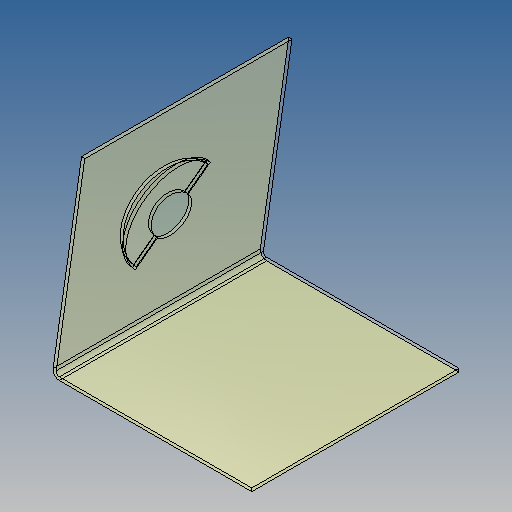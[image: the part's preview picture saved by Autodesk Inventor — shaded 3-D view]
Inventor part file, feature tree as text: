
AUTODESK INVENTOR PART (.ipt)
format: ipt  version: 2017 (Build 210142000, 142)  size: 194,560 bytes
history: native  units: mm
features: other x4, sketch x3, extrude x3, thicken_offset x1, sheet_metal_op x1, reference x1
ambient origin geometry x8: Origin, YZ Plane, XZ Plane, XY Plane, X Axis, Y Axis, Z Axis, Center Point
bodies: Solid1 (feature_tree)
feature tree (13):
  thicken_offset  "Thicken1"
  sketch  "Sketch2"  dims[d2=48.0mm d3=45.0mm]
  extrude  "Extrusion1"  Depth=49.0mm
  sheet_metal_op  "Fold1"
  extrude  "Extrusion2"  Depth=45.0mm
  sketch  "Sketch1"  dims[d0=49.0mm d1=49.0mm]
  reference  "Reference1"
  other  "Srf1"
  sketch  "Sketch3"  dims[d4=6.0mm d5=3.0mm d6=98.0mm d7=0.0mm d8=1.5mm d9=1.0mm d10=315.0deg d11=21.0mm d12=8.0mm d13=98.0mm d14=0.0mm d15=1.5mm d16=0.75mm d17=3.0mm d18=1.5mm d19=1.745329mm d20=1.5mm d21=18.0mm d22=98.0mm d23=0.0mm]
  extrude  "ExtrusionSrf1"  Depth=3.0mm
  other  "<userpath>\Dropbox\multiactuador\case.iam"
  other  "case.iam"
  other  "remache:3"
